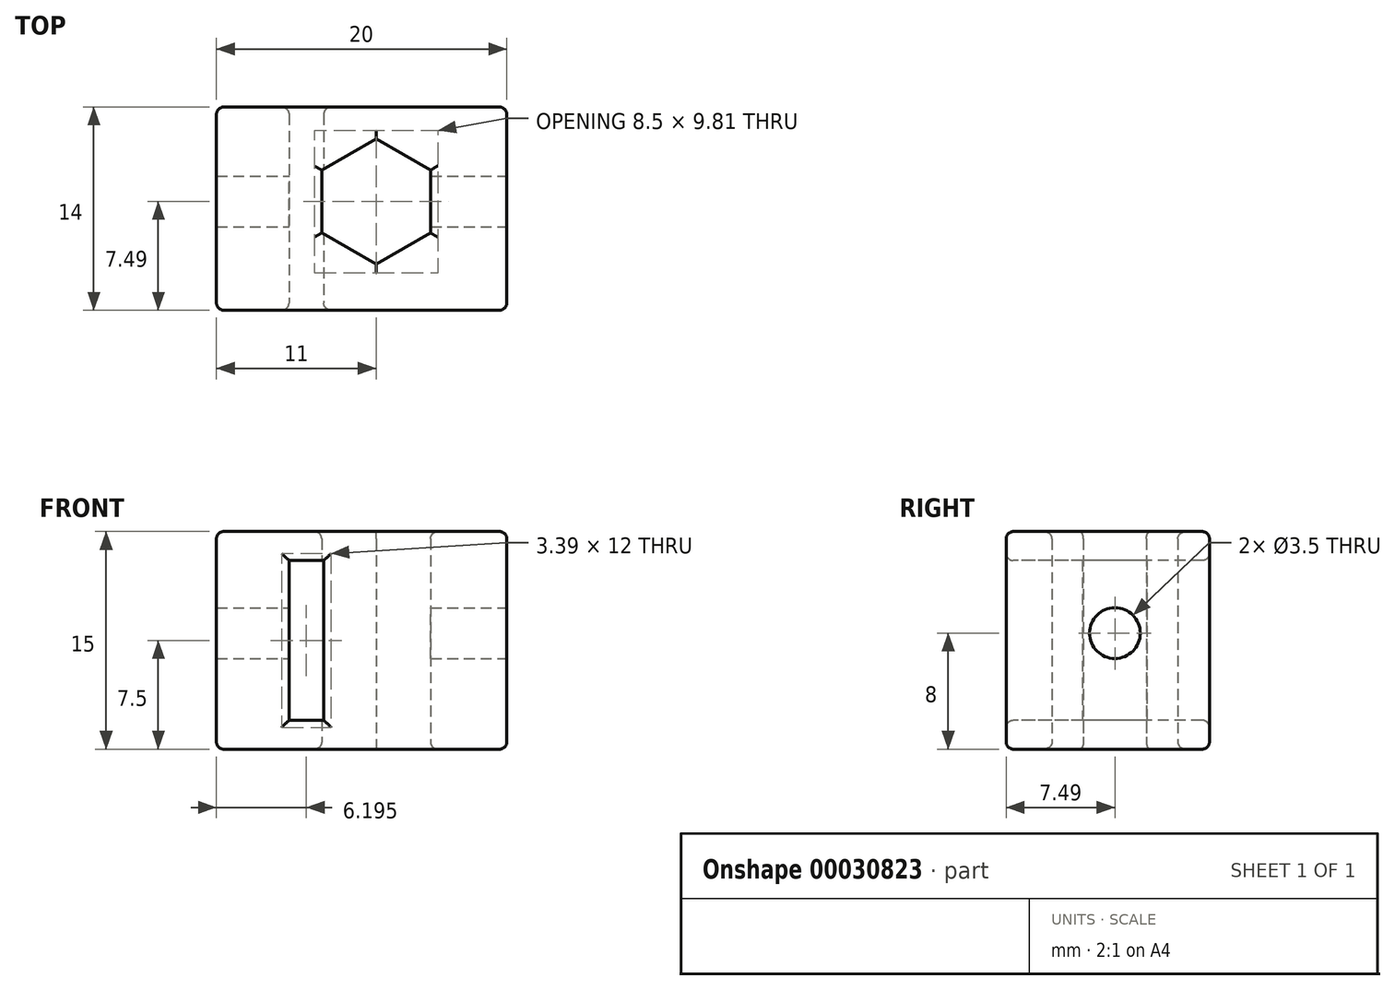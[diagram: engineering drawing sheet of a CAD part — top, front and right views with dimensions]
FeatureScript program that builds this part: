
annotation { "Feature Type Name" : "Feature", "Feature Type Description" : "" }
export const myFeature = defineFeature(function(context is Context, id is Id, definition is map)
    precondition{}
    {
        {
            var Q0;
            Q0=qCreatedBy(makeId("Top.planeOp"),FACE);
            var sketch = newSketch(context, id + "F0", { "sketchPlane" : qUnion([Q0])});
            skPoint(sketch, "E0.rect.middle", {"position": v(0, 0) * mm});
            skLineSegment(sketch, "E1", {"start": v(-11, 6.5) * mm, "end": v(9, 6.5) * mm});
            skLineSegment(sketch, "E2", {"start": v(9, 6.5) * mm, "end": v(9, -7.5) * mm});
            skLineSegment(sketch, "E3", {"start": v(9, -7.5) * mm, "end": v(-11, -7.5) * mm});
            skLineSegment(sketch, "E4", {"start": v(-11, -7.5) * mm, "end": v(-11, 6.5) * mm});
            skCircle(sketch, "E5.cCircle", {"center": v(0, 0) * mm, "radius": 4.33 * mm, "construction": true});
            skLineSegment(sketch, "E5.0", {"start": v(0, -4.33) * mm, "end": v(-3.75, -2.17) * mm});
            skLineSegment(sketch, "E5.1", {"start": v(-3.75, -2.17) * mm, "end": v(-3.75, 2.17) * mm});
            skLineSegment(sketch, "E5.2", {"start": v(-3.75, 2.17) * mm, "end": v(0, 4.33) * mm});
            skLineSegment(sketch, "E5.3", {"start": v(0, 4.33) * mm, "end": v(3.75, 2.17) * mm});
            skLineSegment(sketch, "E5.4", {"start": v(3.75, 2.17) * mm, "end": v(3.75, -2.17) * mm});
            skLineSegment(sketch, "E5.5", {"start": v(3.75, -2.17) * mm, "end": v(0, -4.33) * mm});
            skSolve(sketch);
        }
        {
            var Q0;
            Q0 = qSketchRegion(id + "F0", true);
            extrude(context, id + "F1", {"entities" : qUnion([Q0]), "depth" : 15 * mm});
        }
        {
            var Q0;
            Q0=makeQuery(id+"F1.opExtrude","SWEPT_FACE",FACE,{"disambiguationData":[OSD([sQuery(id+"F0.wireOp",EDGE,"E3")])]});
            var sketch = newSketch(context, id + "F2", { "sketchPlane" : qUnion([Q0])});
            skLineSegment(sketch, "E6.bottom", {"start": v(-6, 13) * mm, "end": v(-3.6, 13) * mm});
            skLineSegment(sketch, "E6.top", {"start": v(-6, 2) * mm, "end": v(-3.6, 2) * mm});
            skLineSegment(sketch, "E6.left", {"start": v(-6, 13) * mm, "end": v(-6, 2) * mm});
            skLineSegment(sketch, "E6.right", {"start": v(-3.6, 13) * mm, "end": v(-3.6, 2) * mm});
            skSolve(sketch);
        }
        {
            var Q0;
            Q0 = qSketchRegion(id + "F2", true);
            extrude(context, id + "F3", {"entities" : qUnion([Q0]), "operationType" : NewBodyOperationType.REMOVE, "endBound" : BoundingType.THROUGH_ALL, "oppositeDirection" : true, "depth" : 25 * mm});
        }
        {
            var Q0;
            Q0=makeQuery(id+"F1.opExtrude","SWEPT_FACE",FACE,{"disambiguationData":[OSD([sQuery(id+"F0.wireOp",EDGE,"E4")])]});
            var sketch = newSketch(context, id + "F4", { "sketchPlane" : qUnion([Q0])});
            skCircle(sketch, "E7", {"center": v(0, 8) * mm, "radius": 1.75 * mm});
            skSolve(sketch);
        }
        {
            var Q0;
            Q0=makeQuery(id+"F1.opExtrude","SWEPT_FACE",FACE,{"disambiguationData":[OSD([sQuery(id+"F0.wireOp",EDGE,"E3")])]});
            var Q1;
            Q1=makeQuery(id+"F1.opExtrude","SWEPT_FACE",FACE,{"disambiguationData":[OSD([sQuery(id+"F0.wireOp",EDGE,"E1")])]});
            var Q2;
            Q2=makeQuery(id+"F1.opExtrude","CAP_FACE",FACE,{"disambiguationData":[OSD([sQuery(id+"F0.wireOp",EDGE,"E1"),sQuery(id+"F0.wireOp",EDGE,"E2"),sQuery(id+"F0.wireOp",EDGE,"E3"),sQuery(id+"F0.wireOp",EDGE,"E4"),sQuery(id+"F0.wireOp",EDGE,"E5.0"),sQuery(id+"F0.wireOp",EDGE,"E5.1"),sQuery(id+"F0.wireOp",EDGE,"E5.2"),sQuery(id+"F0.wireOp",EDGE,"E5.3"),sQuery(id+"F0.wireOp",EDGE,"E5.4"),sQuery(id+"F0.wireOp",EDGE,"E5.5")])],"isStart":false});
            var Q3;
            Q3=makeQuery(id+"F1.opExtrude","CAP_FACE",FACE,{"disambiguationData":[OSD([sQuery(id+"F0.wireOp",EDGE,"E1"),sQuery(id+"F0.wireOp",EDGE,"E2"),sQuery(id+"F0.wireOp",EDGE,"E3"),sQuery(id+"F0.wireOp",EDGE,"E4"),sQuery(id+"F0.wireOp",EDGE,"E5.0"),sQuery(id+"F0.wireOp",EDGE,"E5.1"),sQuery(id+"F0.wireOp",EDGE,"E5.2"),sQuery(id+"F0.wireOp",EDGE,"E5.3"),sQuery(id+"F0.wireOp",EDGE,"E5.4"),sQuery(id+"F0.wireOp",EDGE,"E5.5")])],"isStart":true});
            fillet(context, id + "F5", {"entities" : qUnion([Q0, Q1, Q2, Q3]), "radius" : .5 * mm, "tangentPropagation" : true, "allowEdgeOverflow" : false});
        }
        {
            var Q0;
            Q0 = qSketchRegion(id + "F4", true);
            extrude(context, id + "F6", {"entities" : qUnion([Q0]), "operationType" : NewBodyOperationType.REMOVE, "endBound" : BoundingType.THROUGH_ALL, "depth" : 50 * mm, "hasSecondDirection" : true, "secondDirectionBound" : SecondDirectionBoundingType.THROUGH_ALL, "secondDirectionOppositeDirection" : true, "secondDirectionDepth" : 25 * mm});
        }
    });
